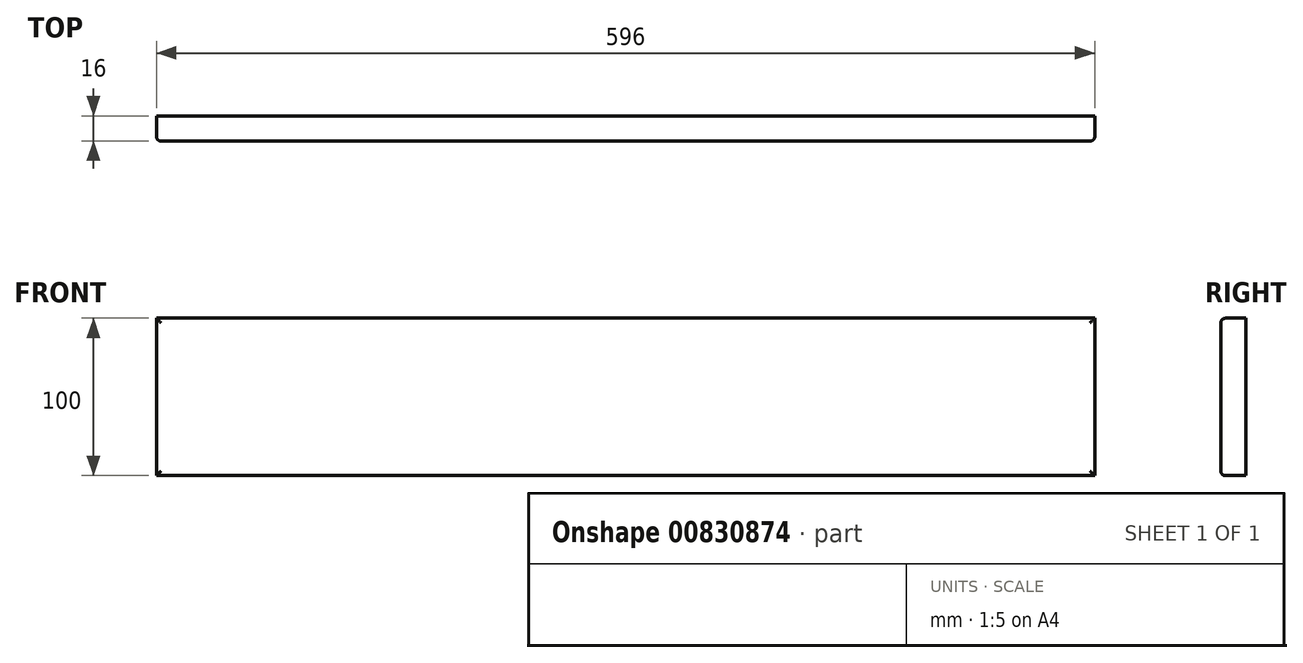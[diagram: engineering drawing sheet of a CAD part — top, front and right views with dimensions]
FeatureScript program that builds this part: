
annotation { "Feature Type Name" : "Feature", "Feature Type Description" : "" }
export const myFeature = defineFeature(function(context is Context, id is Id, definition is map)
    precondition{}
    {
        {
            var Q0;
            Q0=qCreatedBy(makeId("Front.planeOp"),FACE);
            var sketch = newSketch(context, id + "F0", { "sketchPlane" : qUnion([Q0])});
            skLineSegment(sketch, "E0.bottom", {"start": v(0, 0) * mm, "end": v(53.67, 0) * mm});
            skLineSegment(sketch, "E0.top", {"start": v(0, 36.38) * mm, "end": v(53.67, 36.38) * mm});
            skLineSegment(sketch, "E0.left", {"start": v(0, 0) * mm, "end": v(0, 36.38) * mm});
            skLineSegment(sketch, "E0.right", {"start": v(53.67, 0) * mm, "end": v(53.67, 36.38) * mm});
            skSolve(sketch);
        }
        {
            var Q0;
            Q0=makeQuery(id+"F0.imprint","IMPRINT",FACE,{"disambiguationData":[TD([[makeQuery(id+"F0.imprint","IMPRINT",EDGE,{"derivedFrom":sQuery(id+"F0.wireOp",EDGE,"E0.bottom")}),1.0]])]});
            extrude(context, id + "F1", {"entities" : qUnion([Q0]), "depth" : 16 * mm, "offsetDistance" : 25.4 * mm});
        }
        {
            var Q0;
            Q0=makeQuery(id+"F1.opExtrude","SWEPT_FACE",FACE,{"disambiguationData":[OSD([sQuery(id+"F0.wireOp",EDGE,"E0.left")])]});
            extrude(context, id + "F2", {"entities" : qUnion([Q0]), "operationType" : NewBodyOperationType.ADD, "oppositeDirection" : true, "depth" : 396 * mm, "offsetDistance" : 25 * mm});
        }
        {
            var Q0;
            {var subQ0=sQuery(id+"F0.wireOp",EDGE,"E0.bottom");Q0=makeQuery(id+"F2.boolean.opBoolean","MERGE",FACE,{"derivedFrom":[makeQuery(id+"F1.opExtrude","SWEPT_FACE",FACE,{"disambiguationData":[OSD([subQ0])]}),makeQuery(id+"F2.opExtrude","SWEPT_FACE",FACE,{"disambiguationData":[OSD([subQ0,sQuery(id+"F0.wireOp",EDGE,"E0.left")])]})]});}
            extrude(context, id + "F3", {"entities" : qUnion([Q0]), "operationType" : NewBodyOperationType.ADD, "oppositeDirection" : true, "depth" : 100 * mm, "offsetDistance" : 25 * mm});
        }
        {
            var Q0;
            {var subQ0=sQuery(id+"F0.wireOp",EDGE,"E0.left");var subQ1=sQuery(id+"F0.wireOp",EDGE,"E0.bottom");Q0=makeQuery(id+"F3.boolean.opBoolean","MERGE",FACE,{"derivedFrom":[makeQuery(id+"F2.opExtrude","CAP_FACE",FACE,{"disambiguationData":[OSD([subQ0])],"isStart":false}),makeQuery(id+"F3.opExtrude","SWEPT_FACE",FACE,{"disambiguationData":[OSD([subQ1,subQ0]),TDD([makeQuery(id+"F2.opExtrude","CAP_EDGE",EDGE,{"disambiguationData":[OSD([subQ1,subQ0])],"isStart":false})])]})]});}
            extrude(context, id + "F4", {"entities" : qUnion([Q0]), "operationType" : NewBodyOperationType.ADD, "depth" : 200 * mm, "offsetDistance" : 25 * mm});
        }
        {
            var Q0;
            {var subQ0=sQuery(id+"F0.wireOp",EDGE,"E0.left");var subQ1=sQuery(id+"F0.wireOp",EDGE,"E0.bottom");var subQ2=makeQuery(id+"F1.opExtrude","CAP_VERTEX",VERTEX,{"disambiguationData":[OSD([subQ1,subQ0])],"isStart":false});var subQ3=makeQuery(id+"F1.opExtrude","CAP_EDGE",EDGE,{"disambiguationData":[OSD([subQ0])],"isStart":false});Q0=makeQuery(id+"F4.boolean.opBoolean","MERGE",FACE,{"derivedFrom":[makeQuery(id+"F3.boolean.opBoolean","MERGE",FACE,{"derivedFrom":[makeQuery(id+"F2.boolean.opBoolean","MERGE",FACE,{"derivedFrom":[makeQuery(id+"F1.opExtrude","CAP_FACE",FACE,{"disambiguationData":[OSD([subQ1,sQuery(id+"F0.wireOp",EDGE,"E0.top"),subQ0,sQuery(id+"F0.wireOp",EDGE,"E0.right")])],"isStart":false}),makeQuery(id+"F2.opExtrude","SWEPT_FACE",FACE,{"disambiguationData":[OSD([subQ0]),TDD([subQ3])]})]}),makeQuery(id+"F3.opExtrude","SWEPT_FACE",FACE,{"disambiguationData":[OSD([subQ1,subQ0]),TDD([makeQuery(id+"F2.boolean.opBoolean","MERGE",EDGE,{"derivedFrom":[makeQuery(id+"F1.opExtrude","CAP_EDGE",EDGE,{"disambiguationData":[OSD([subQ1])],"isStart":false}),makeQuery(id+"F2.opExtrude","SWEPT_EDGE",EDGE,{"disambiguationData":[OSD([subQ1,subQ0]),TDD([subQ2])]})]})])]})]}),makeQuery(id+"F4.opExtrude","SWEPT_FACE",FACE,{"disambiguationData":[OSD([subQ1,subQ0]),TDD([makeQuery(id+"F3.boolean.opBoolean","MERGE",EDGE,{"derivedFrom":[makeQuery(id+"F2.opExtrude","CAP_EDGE",EDGE,{"disambiguationData":[OSD([subQ0]),TDD([subQ3])],"isStart":false}),makeQuery(id+"F3.opExtrude","SWEPT_EDGE",EDGE,{"disambiguationData":[OSD([subQ1,subQ0]),TDD([makeQuery(id+"F2.opExtrude","CAP_VERTEX",VERTEX,{"disambiguationData":[OSD([subQ1,subQ0]),TDD([subQ2])],"isStart":false})])]})]})])]})]});}
            fillet(context, id + "F5", {"entities" : qUnion([Q0]), "radius" : 3 * mm, "tangentPropagation" : true, "allowEdgeOverflow" : false});
        }
    });
